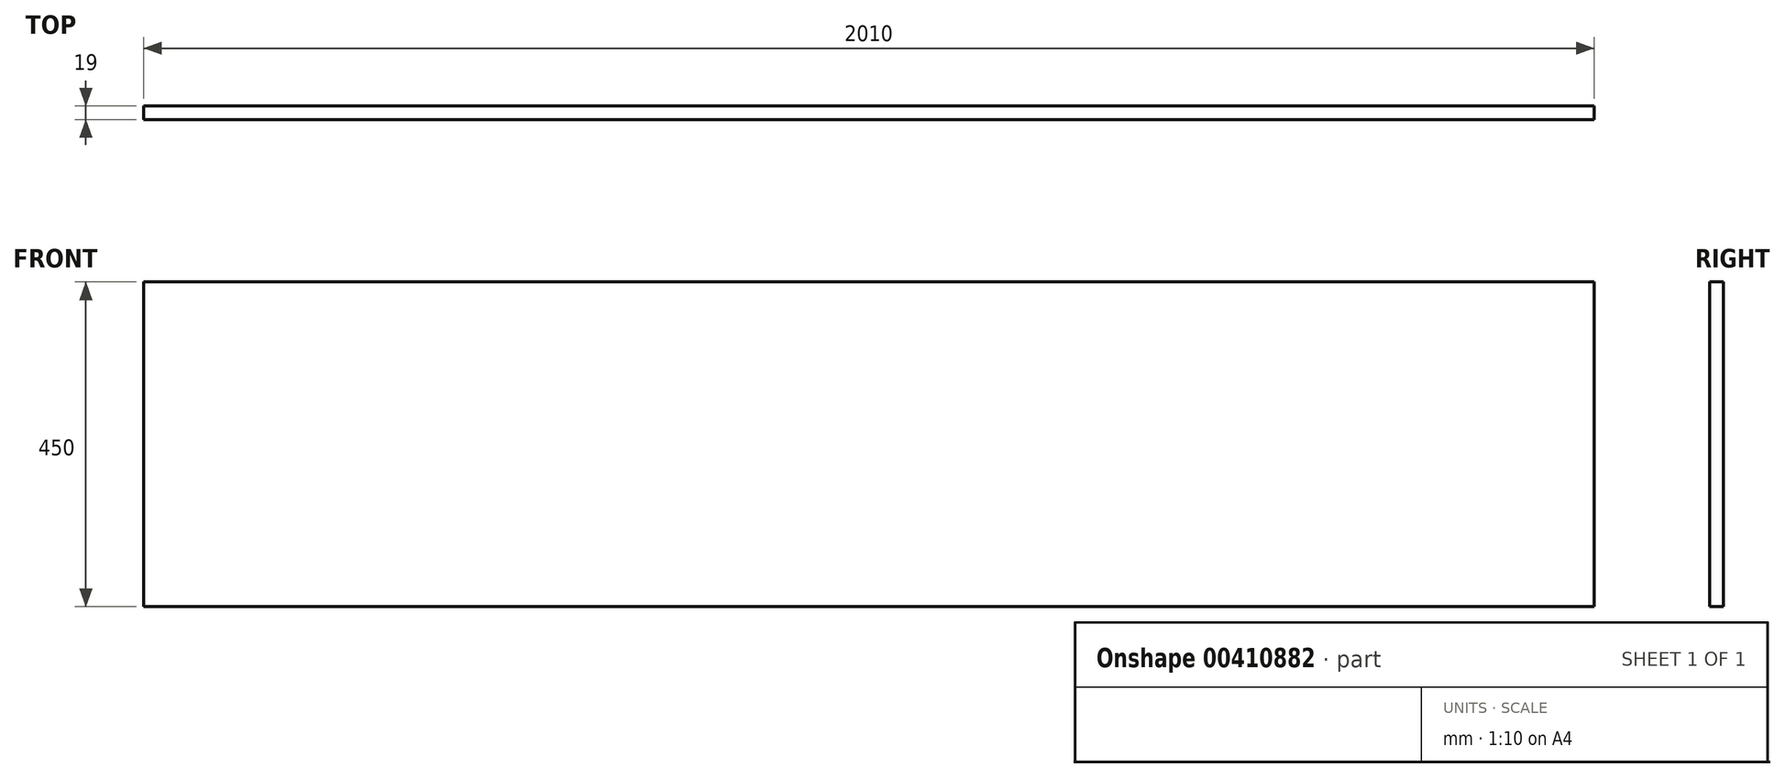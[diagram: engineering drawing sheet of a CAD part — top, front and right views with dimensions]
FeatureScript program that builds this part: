
annotation { "Feature Type Name" : "Feature", "Feature Type Description" : "" }
export const myFeature = defineFeature(function(context is Context, id is Id, definition is map)
    precondition{}
    {
        {
            var Q0;
            Q0=qCreatedBy(makeId("Top.planeOp"),FACE);
            var sketch = newSketch(context, id + "F0", { "sketchPlane" : qUnion([Q0])});
            skLineSegment(sketch, "E0.bottom", {"start": v(-1013.95, 22.5) * mm, "end": v(996.05, 22.5) * mm});
            skLineSegment(sketch, "E0.top", {"start": v(-1013.95, 3.5) * mm, "end": v(996.05, 3.5) * mm});
            skLineSegment(sketch, "E0.left", {"start": v(-1013.95, 22.5) * mm, "end": v(-1013.95, 3.5) * mm});
            skLineSegment(sketch, "E0.right", {"start": v(996.05, 22.5) * mm, "end": v(996.05, 3.5) * mm});
            skSolve(sketch);
        }
        {
            var Q0;
            Q0=qSketchRegion(id+"F0",true);
            extrude(context, id + "F1", {"entities" : qUnion([Q0]), "depth" : 450 * mm});
        }
    });
